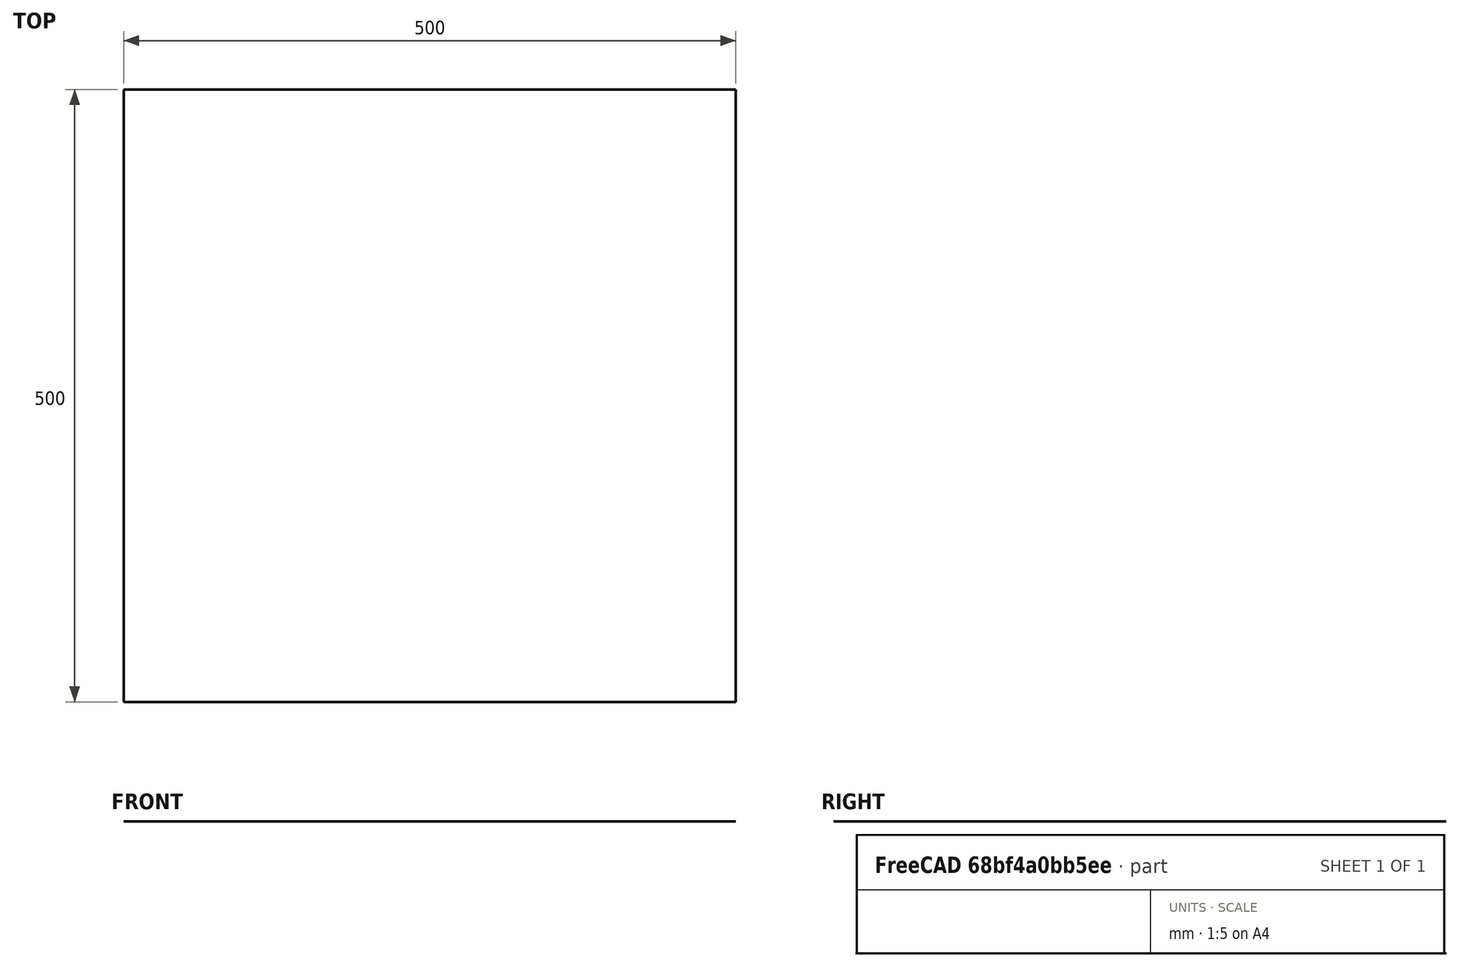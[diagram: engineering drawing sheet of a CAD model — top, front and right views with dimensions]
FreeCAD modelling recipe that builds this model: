
FCSTD DOCUMENT  (FreeCAD 0.19R16830 +1504 (Git))
Label: york_jaw_mechanism
License: CreativeCommons Attribution
LicenseURL: http://creativecommons.org/licenses/by/4.0/
objects: App::FeaturePython×28, Part::FeaturePython×10, Part::Part2DObjectPython×8
note: 17 computed .brp shape members not serialized (recipe doc carries the construction recipe); baked Part::Feature solids carry a one-line shape summary decoded from their .brp

FEATURE [Part::FeaturePython] Workplane  # WARN: FeaturePython — macro-defined, semantics opaque (R4)
  Fixed = true
  Length = 500
  Width = 500
FEATURE [Part::Part2DObjectPython] Line  label="york"  # Draft 2D object (typed FeaturePython)
  Area = 0
  ChamferSize = 0
  Closed = false
  End = (59.448,-132.705,-1.55386e-05)
  FilletRadius = 0
  Length = 120
  MakeFace = true
  Placement = pos=(-81.5583,-12.053,0) rot=(0,0,1;0rad)
  Points = (2) [(21.0064,-120.652,-1.55386e-05),(141.006,-120.652,-1.55386e-05)]
  Start = (-60.552,-132.705,-1.55386e-05)
  Subdivisions = 0
FEATURE [Part::Part2DObjectPython] Wire  label="cutter"  # Draft 2D object (typed FeaturePython)
  Area = 0
  ChamferSize = 0
  Closed = false
  End = (-175.3,-54.0007,0)
  FilletRadius = 0
  Length = 204.384
  MakeFace = true
  Placement = pos=(-61.4212,98.2375,0) rot=(0,0,1;0rad)
  Points = (3) [(0,0,0),(-37.1605,-111.482,0),(-113.879,-152.238,0)]
  Start = (-61.4212,98.2375,0)
  Subdivisions = 0
FEATURE [Part::Part2DObjectPython] Wire001  label="pressurer"  # Draft 2D object (typed FeaturePython)
  Area = 0
  ChamferSize = 0
  Closed = false
  End = (141.164,-59.9944,0)
  FilletRadius = 0
  Length = 204.492
  MakeFace = true
  Placement = pos=(28.4833,94.6414,0) rot=(0,0,1;0rad)
  Points = (3) [(0,0,0),(37.1606,-111.482,0),(112.68,-154.636,0)]
  Start = (28.4833,94.6414,0)
  Subdivisions = 0
FEATURE [Part::Part2DObjectPython] Line001  label="cutter_link"  # Draft 2D object (typed FeaturePython)
  Area = 0
  ChamferSize = 0
  Closed = false
  End = (-45.8377,-110.341,0)
  FilletRadius = 0
  Length = 124.448
  MakeFace = true
  Placement = pos=(-162.114,-65.988,0) rot=(0,0,1;0rad)
  Points = (2) [(0,0,0),(116.276,-44.3529,0)]
  Start = (-162.114,-65.988,0)
  Subdivisions = 0
FEATURE [Part::Part2DObjectPython] Line002  label="pressurer_link"  # Draft 2D object (typed FeaturePython)
  Area = 0
  ChamferSize = 0
  Closed = false
  End = (109.997,-77.9753,0)
  FilletRadius = 0
  Length = 121.024
  MakeFace = true
  Placement = pos=(-6.27972,-111.54,0) rot=(0,0,1;0rad)
  Points = (2) [(0,0,0),(116.276,33.5644,0)]
  Start = (-6.27972,-111.54,0)
  Subdivisions = 0
FEATURE [Part::Part2DObjectPython] Line003  label="axis"  # Draft 2D object (typed FeaturePython)
  Area = 0
  ChamferSize = 0
  Closed = false
  End = (0,-300,0)
  FilletRadius = 0
  Length = 300
  MakeFace = true
  Points = (2) [(0,0,0),(0,-300,0)]
  Start = (0,0,0)
  Subdivisions = 0
FEATURE [Part::Part2DObjectPython] Circle  # Draft 2D object (typed FeaturePython)
  Area = 0
  FirstAngle = 0
  LastAngle = 0
  MakeFace = false
  Placement = pos=(-98.5817,-13.2441,0) rot=(0,0,1;0rad)
  Radius = 70.9482
FEATURE [Part::Part2DObjectPython] Circle001  # Draft 2D object (typed FeaturePython)
  Area = 0
  FirstAngle = 0
  LastAngle = 0
  MakeFace = false
  Placement = pos=(65.6439,-16.8402,0) rot=(0,0,1;0rad)
  Radius = 82.0654
FEATURE [Part::FeaturePython] Parts  # WARN: FeaturePython — macro-defined, semantics opaque (R4)
  Group = -> [Workplane,Line,Wire,Wire001,Line001,Line002,Line003,Circle,Circle001]
  GroupMode = 0
FEATURE [Part::FeaturePython] Assembly  # WARN: FeaturePython — macro-defined, semantics opaque (R4)
  AutoRelax = true
  BuildShape = 0
  Freeze = false
  Group = -> [Constraints,Elements,Parts]
  GroupMode = 1
  SolverType = 1
  Verbose = false
  _SolverType = 1
  _Version = 1
FEATURE [App::FeaturePython] Constraints  # WARN: FeaturePython — macro-defined, semantics opaque (R4)
  Group = -> [Constraint,Constraint001,Constraint002,Constraint003,Constraint004,Constraint005,Constraint006,Constraint007,Constraint008,Constraint009,Constraint010,Constraint011]
  GroupMode = 1
  _Version = 1
FEATURE [App::FeaturePython] Elements  # WARN: FeaturePython — macro-defined, semantics opaque (R4)
  Group = -> [_Element,_Element001,_Element002,_Element003,_Element004,_Element005,_Element006]
  GroupMode = 1
FEATURE [App::FeaturePython] Constraint  label="SketchPlane"  # WARN: FeaturePython — macro-defined, semantics opaque (R4)
  ConstraintType = 28
  Disabled = false
  Group = -> [ElementLink]
  GroupMode = 1
  _ConstraintType = 38
  _Parent = -> Constraints
FEATURE [App::FeaturePython] ElementLink  label="_Element"  # link proxy (typed FeaturePython)
  LinkTransform = true
  LinkedObject = -> _Element
  _Parent = -> Constraint
FEATURE [Part::FeaturePython] _Element  # link proxy (typed FeaturePython)
  Detach = false
  LinkTransform = true
  LinkedObject = -> Workplane [Face1]
  _Parent = -> Elements
FEATURE [App::FeaturePython] Constraint001  label="LineLength"  # WARN: FeaturePython — macro-defined, semantics opaque (R4)
  ConstraintType = 29
  Disabled = false
  Group = -> [ElementLink001]
  GroupMode = 1
  Length = 120
  _ConstraintType = 34
  _Parent = -> Constraints
FEATURE [App::FeaturePython] ElementLink001  label="_Element001"  # link proxy (typed FeaturePython)
  LinkTransform = true
  LinkedObject = -> _Element001
  _Parent = -> Constraint001
FEATURE [Part::FeaturePython] _Element001  # link proxy (typed FeaturePython)
  Detach = false
  LinkTransform = true
  LinkedObject = -> Line [Edge1]
  _Parent = -> Elements
FEATURE [App::FeaturePython] Constraint002  label="Diameter"  # WARN: FeaturePython — macro-defined, semantics opaque (R4)
  ConstraintType = 36
  Diameter = 120
  Disabled = false
  Group = -> [ElementLink002]
  GroupMode = 1
  _ConstraintType = 25
  _Parent = -> Constraints
FEATURE [App::FeaturePython] ElementLink002  label="_Element002"  # link proxy (typed FeaturePython)
  LinkTransform = true
  LinkedObject = -> _Element002
  _Parent = -> Constraint002
FEATURE [Part::FeaturePython] _Element002  # link proxy (typed FeaturePython)
  Detach = false
  LinkTransform = true
  LinkedObject = -> Circle [Edge1]
  _Parent = -> Elements
FEATURE [App::FeaturePython] Constraint003  label="Diameter"  # WARN: FeaturePython — macro-defined, semantics opaque (R4)
  ConstraintType = 36
  Diameter = 120
  Disabled = false
  Group = -> [ElementLink003]
  GroupMode = 1
  _ConstraintType = 25
  _Parent = -> Constraints
FEATURE [App::FeaturePython] ElementLink003  label="_Element003"  # link proxy (typed FeaturePython)
  LinkTransform = true
  LinkedObject = -> _Element003
  _Parent = -> Constraint003
FEATURE [Part::FeaturePython] _Element003  # link proxy (typed FeaturePython)
  Detach = false
  LinkTransform = true
  LinkedObject = -> Circle001 [Edge1]
  _Parent = -> Elements
FEATURE [App::FeaturePython] Constraint004  label="LineLength"  # WARN: FeaturePython — macro-defined, semantics opaque (R4)
  ConstraintType = 29
  Disabled = false
  Group = -> [ElementLink004]
  GroupMode = 1
  Length = 174.83
  _ConstraintType = 34
  _Parent = -> Constraints
FEATURE [App::FeaturePython] ElementLink004  label="_Element004"  # link proxy (typed FeaturePython)
  LinkTransform = true
  LinkedObject = -> _Element004
  _Parent = -> Constraint004
FEATURE [Part::FeaturePython] _Element004  # link proxy (typed FeaturePython)
  Detach = false
  LinkTransform = true
  LinkedObject = -> Wire [Edge1]
  _Parent = -> Elements
FEATURE [App::FeaturePython] Constraint005  label="LineLength"  # WARN: FeaturePython — macro-defined, semantics opaque (R4)
  ConstraintType = 29
  Disabled = false
  Group = -> [ElementLink005]
  GroupMode = 1
  Length = 174.83
  _ConstraintType = 34
  _Parent = -> Constraints
FEATURE [App::FeaturePython] ElementLink005  label="_Element004"  # link proxy (typed FeaturePython)
  LinkTransform = true
  LinkedObject = -> _Element004
  _Parent = -> Constraint005
FEATURE [App::FeaturePython] Constraint006  label="LineLength"  # WARN: FeaturePython — macro-defined, semantics opaque (R4)
  ConstraintType = 29
  Disabled = false
  Group = -> [ElementLink006]
  GroupMode = 1
  Length = 100
  _ConstraintType = 34
  _Parent = -> Constraints
FEATURE [App::FeaturePython] ElementLink006  label="_Element005"  # link proxy (typed FeaturePython)
  LinkTransform = true
  LinkedObject = -> _Element005
  _Parent = -> Constraint006
FEATURE [Part::FeaturePython] _Element005  # link proxy (typed FeaturePython)
  Detach = false
  LinkTransform = true
  LinkedObject = -> Wire [Edge2]
  _Parent = -> Elements
FEATURE [App::FeaturePython] Constraint007  label="MeasureAngle"  # WARN: FeaturePython — macro-defined, semantics opaque (R4)
  Angle = 43.5856
  ConstraintType = 44
  Disabled = false
  Group = -> [ElementLink007,ElementLink008]
  GroupMode = 1
  Supplement = false
  _ConstraintType = 43
  _Parent = -> Constraints
  expr: .Label2 = .Angle
FEATURE [App::FeaturePython] ElementLink007  label="_Element004"  # link proxy (typed FeaturePython)
  LinkTransform = true
  LinkedObject = -> _Element004
  _Parent = -> Constraint007
FEATURE [App::FeaturePython] ElementLink008  label="_Element005"  # link proxy (typed FeaturePython)
  LinkTransform = true
  LinkedObject = -> _Element005
  _Parent = -> Constraint007
FEATURE [App::FeaturePython] Constraint008  label="LineHorizontal"  # WARN: FeaturePython — macro-defined, semantics opaque (R4)
  ConstraintType = 25
  Disabled = false
  Group = -> [ElementLink009]
  GroupMode = 1
  _ConstraintType = 23
  _Parent = -> Constraints
FEATURE [App::FeaturePython] ElementLink009  label="_Element001"  # link proxy (typed FeaturePython)
  LinkTransform = true
  LinkedObject = -> _Element001
  _Parent = -> Constraint008
FEATURE [App::FeaturePython] Constraint009  label="LineVertical"  # WARN: FeaturePython — macro-defined, semantics opaque (R4)
  ConstraintType = 26
  Disabled = false
  Group = -> [ElementLink010]
  GroupMode = 1
  _ConstraintType = 24
  _Parent = -> Constraints
FEATURE [App::FeaturePython] ElementLink010  label="_Element006"  # link proxy (typed FeaturePython)
  LinkTransform = true
  LinkedObject = -> _Element006
  _Parent = -> Constraint009
FEATURE [Part::FeaturePython] _Element006  # link proxy (typed FeaturePython)
  Detach = false
  LinkTransform = true
  LinkedObject = -> Line003 [Edge1]
  _Parent = -> Elements
FEATURE [App::FeaturePython] Constraint010  label="Locked"  # WARN: FeaturePython — macro-defined, semantics opaque (R4)
  ConstraintType = 0
  Disabled = false
  Group = -> [ElementLink011]
  GroupMode = 1
  _ConstraintType = 0
  _Parent = -> Constraints
FEATURE [App::FeaturePython] ElementLink011  label="_Element006"  # link proxy (typed FeaturePython)
  LinkTransform = true
  LinkedObject = -> _Element006
  _Parent = -> Constraint010
FEATURE [App::FeaturePython] Constraint011  label="MeasureAngle"  # WARN: FeaturePython — macro-defined, semantics opaque (R4)
  Angle = 43.5856
  ConstraintType = 44
  Disabled = false
  Group = -> [ElementLink012,ElementLink013]
  GroupMode = 1
  Supplement = false
  _ConstraintType = 43
  _Parent = -> Constraints
  expr: .Label2 = .Angle
FEATURE [App::FeaturePython] ElementLink012  label="_Element004"  # link proxy (typed FeaturePython)
  LinkTransform = true
  LinkedObject = -> _Element004
  _Parent = -> Constraint011
FEATURE [App::FeaturePython] ElementLink013  label="_Element005"  # link proxy (typed FeaturePython)
  LinkTransform = true
  LinkedObject = -> _Element005
  _Parent = -> Constraint011
